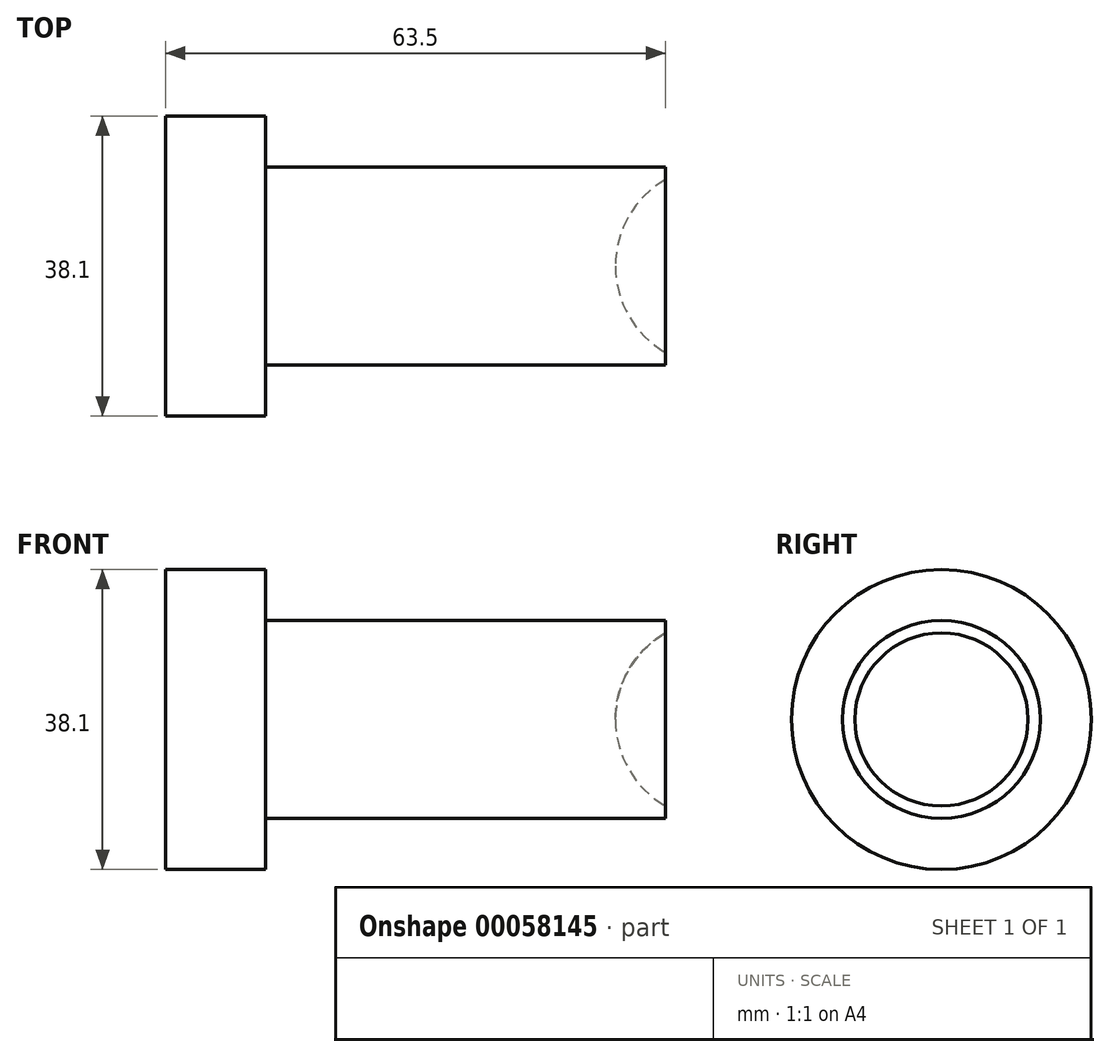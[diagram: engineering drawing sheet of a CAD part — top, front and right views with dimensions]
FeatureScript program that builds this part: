
annotation { "Feature Type Name" : "Feature", "Feature Type Description" : "" }
export const myFeature = defineFeature(function(context is Context, id is Id, definition is map)
    precondition{}
    {
        {
            var Q0;
            Q0=qCreatedBy(makeId("Front.planeOp"),FACE);
            var sketch = newSketch(context, id + "F0", { "sketchPlane" : qUnion([Q0])});
            skLineSegment(sketch, "E0", {"start": v(0, 0) * mm, "end": v(0, 19.05) * mm});
            skLineSegment(sketch, "E1", {"start": v(0, 19.05) * mm, "end": v(12.7, 19.05) * mm});
            skLineSegment(sketch, "E2", {"start": v(12.7, 19.05) * mm, "end": v(12.7, 0) * mm});
            skLineSegment(sketch, "E3", {"start": v(12.7, 0) * mm, "end": v(0, 0) * mm});
            skLineSegment(sketch, "E4", {"start": v(12.7, 0) * mm, "end": v(63.5, 0) * mm});
            skLineSegment(sketch, "E5", {"start": v(63.5, 0) * mm, "end": v(63.5, 12.57) * mm});
            skLineSegment(sketch, "E6", {"start": v(63.5, 12.57) * mm, "end": v(12.7, 12.57) * mm});
            skSolve(sketch);
        }
        {
            var Q0;
            Q0 = qSketchRegion(id + "F0", true);
            var Q1;
            Q1=sQuery(id+"F0.wireOp",EDGE,"E3");
            revolve(context, id + "F1", {"entities" : qUnion([Q0]), "axis" : qUnion([Q1]), "revolveType" : RevolveType.FULL});
        }
        {
            var Q0;
            Q0=qCreatedBy(makeId("Front.planeOp"),FACE);
            var sketch = newSketch(context, id + "F2", { "sketchPlane" : qUnion([Q0])});
            skArc(sketch, "E7", {"start": v(63.5, 11) * mm, "mid": v(58.85, 6.35) * mm, "end": v(57.15, 0) * mm});
            skLineSegment(sketch, "E8", {"start": v(57.15, 0) * mm, "end": v(63.5, 0) * mm});
            skLineSegment(sketch, "E9", {"start": v(63.5, 0) * mm, "end": v(63.5, 11) * mm});
            skSolve(sketch);
        }
        {
            var Q0;
            Q0 = qSketchRegion(id + "F2", true);
            var Q1;
            Q1=sQuery(id+"F2.wireOp",EDGE,"E8");
            revolve(context, id + "F3", {"operationType" : NewBodyOperationType.REMOVE, "entities" : qUnion([Q0]), "axis" : qUnion([Q1]), "revolveType" : RevolveType.FULL, "oppositeDirection" : true});
        }
    });
